# Revit family: ledspotrc-linear-e_l150-12w-930_940-30d_541003824300_3926
name_source: partatom
category: Lighting Fixtures
units: mm (PartAtom-declared; Revit-internal decimal feet)

## family parameters
Cut with Voids When Loaded = No
Host = Face
Light Source = No
Part Type = Normal
Room Calculation Point = No
Round Connector Dimension = Use Diameter
Shared = No

## types (1)
- LEDSpotRc-Linear-E L150-12W-930/940-30D (1 x LED, 1080 lm, 4000)
    Apparent Load = 12 VA
    Approval mark = CE
    CIE Flux Codes = 99 100 100 100 100
    Color Rendering = 90
    Color Temperature = 4000
    Control Gear = Electronic ballast
    Default Elevation = 1800 mm
    Description = Spot Linear 12W-1080lm-3/4000K-30°-UGR10
    Frequency = 60 Hz
    Height = 41 mm
    Lamp = 1 x LED
    Lamp Light Flux = 1080 lm
    Lamp count = 1
    Length = 160 mm
    Luminous efficacy = 90 lm/W
    Manufacturer = OPPLE
    ModVariant = No
    Model = 541003824300
    Mounting Place = Ceiling
    Mounting Type = Surface mounted
    Number of Poles = 1
    OnlyDefault = Yes
    Power Factor = 1
    Product Name = LEDSpotRc-Linear-E L150-12W-930/940-30D
    Product group = Ceiling mounted luminaire
    ProductGroupID = 3
    Protection Class = Protection class II
    Protection Degree = IP 20
    RLX_Detail_Level = 1
    RLX_Emergency_Light_Flux = 0 lm
    RLX_Emergency_Type = 0
    RLX_Emergency_Type_DB = No
    RlxData = <blob elided: 152733 chars, md5=32780c32>
    Socket = socket
    Standby Power = 0 W
    System Light Flux = 1080 lm
    System Power = 12 W
    Type Comments = Product without accessories
    Type Image = web_spot_lin_12w.jpg
    URL = http://relux.com
    VarID = ---
    Voltage = 230 V
    Voltage Range = 220-240 V
    Weight = 0.00 kg
    Width = 44 mm

## geometry (parser evidence)
native form markers: Sweep x10
no freeform markers — native parametric forms only
